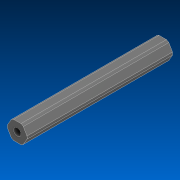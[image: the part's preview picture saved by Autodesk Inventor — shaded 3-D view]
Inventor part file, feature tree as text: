
AUTODESK INVENTOR PART (.ipt)
format: ipt  version: 2022.2 (Build 262287000, 287)  size: 123,392 bytes
history: native  units: in
note: dims shown in document units (in); Inventor stores cm internally (conversion verified against a paired STEP export)
features: extrude x1, sketch x1, other x1
ambient origin geometry x8: Origin, YZ Plane, XZ Plane, XY Plane, X Axis, Y Axis, Z Axis, Center Point
bodies: Solid1 (feature_tree)
feature tree (3):
  extrude  "Extrusion1"  TaperAngle=0.0deg  [1 undecoded]
  sketch  "Sketch1"  dims[d0=32.0in d1=0.0in]
  other  "Cut-Extrude2"
note: 1 required parameter value undecoded (feature->parameter linkage not recoverable at this tier; creation-order binding heuristic only, values carry confidence <= 0.55)
